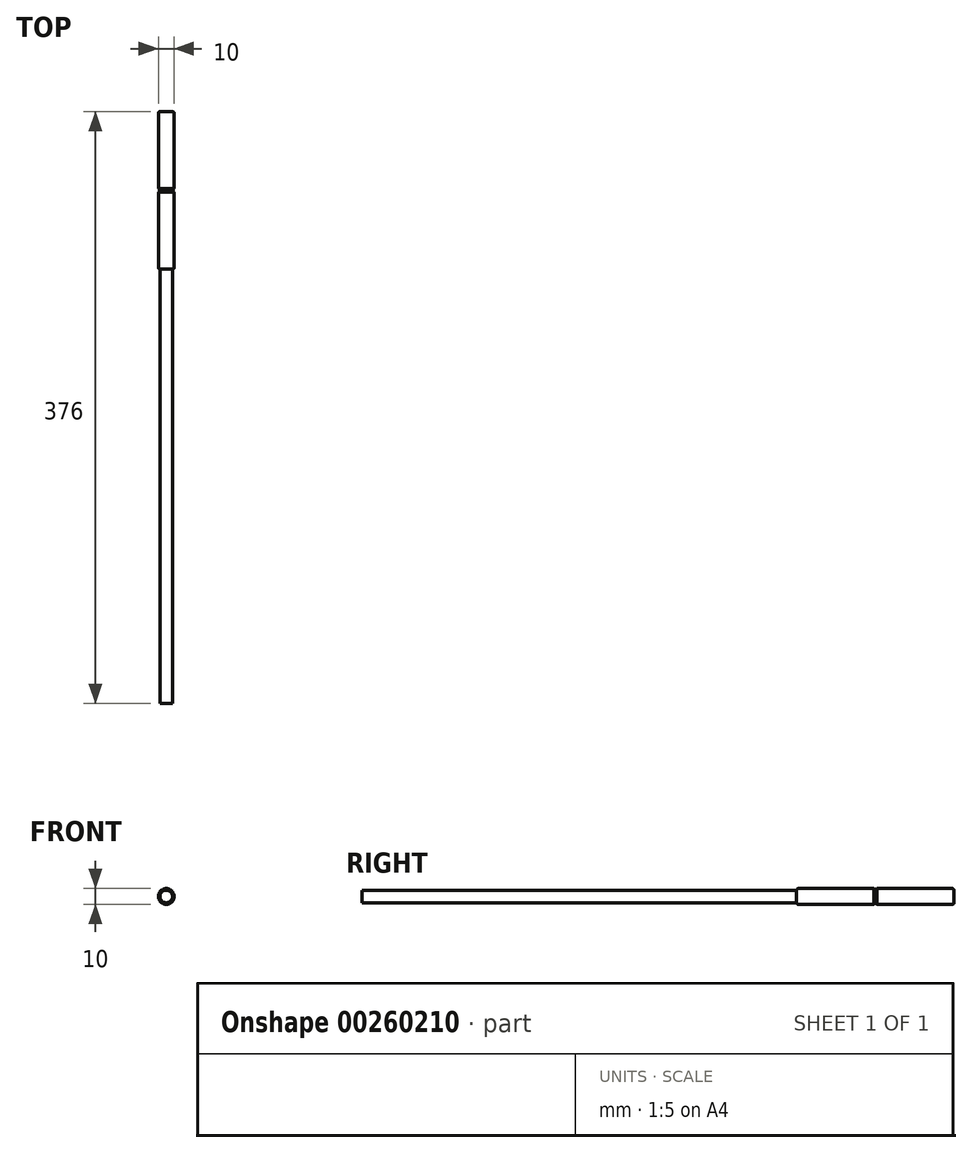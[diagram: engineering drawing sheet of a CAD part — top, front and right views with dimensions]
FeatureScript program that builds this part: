
annotation { "Feature Type Name" : "Feature", "Feature Type Description" : "" }
export const myFeature = defineFeature(function(context is Context, id is Id, definition is map)
    precondition{}
    {
        {
            var Q0;
            Q0=qCreatedBy(makeId("Front.planeOp"),FACE);
            var sketch = newSketch(context, id + "F0", { "sketchPlane" : qUnion([Q0])});
            skCircle(sketch, "E0", {"center": v(0, 0) * mm, "radius": 5 * mm});
            skSolve(sketch);
        }
        {
            var Q0;
            Q0=makeQuery(id+"F0.imprint","IMPRINT",FACE,{"disambiguationData":[TD([[makeQuery(id+"F0.imprint","IMPRINT",EDGE,{"derivedFrom":sQuery(id+"F0.wireOp",EDGE,"E0")}),1.0]])]});
            extrude(context, id + "F1", {"entities" : qUnion([Q0]), "depth" : 50 * mm});
        }
        {
            var Q0;
            Q0=makeQuery(id+"F1.opExtrude","CAP_EDGE",EDGE,{"disambiguationData":[OSD([sQuery(id+"F0.wireOp",EDGE,"E0")])],"isStart":false});
            fillet(context, id + "F2", {"entities" : qUnion([Q0]), "radius" : 1 * mm, "tangentPropagation" : true, "allowEdgeOverflow" : false});
        }
        {
            var Q0;
            Q0=makeQuery(id+"F1.opExtrude","CAP_EDGE",EDGE,{"disambiguationData":[OSD([sQuery(id+"F0.wireOp",EDGE,"E0")])],"isStart":true});
            chamfer(context, id + "F3", {"entities" : qUnion([Q0]), "width" : 1 * mm, "tangentPropagation" : true});
        }
        {
            var Q0;
            Q0=makeQuery(id+"F1.opExtrude","SWEPT_BODY",BODY,{"disambiguationData":[OSD([sQuery(id+"F0.wireOp",EDGE,"E0")])]});
            var Q1;
            Q1=qCreatedBy(makeId("Front.planeOp"),FACE);
            mirror(context, id + "F4", {"entities" : qUnion([Q0]), "mirrorPlane" : qUnion([Q1])});
        }
        {
            var Q0;
            Q0=makeQuery(id+"F1.opExtrude","CAP_FACE",FACE,{"disambiguationData":[OSD([sQuery(id+"F0.wireOp",EDGE,"E0")])],"isStart":false});
            extrude(context, id + "F5", {"entities" : qUnion([Q0]), "depth" : 276 * mm});
        }
    });
